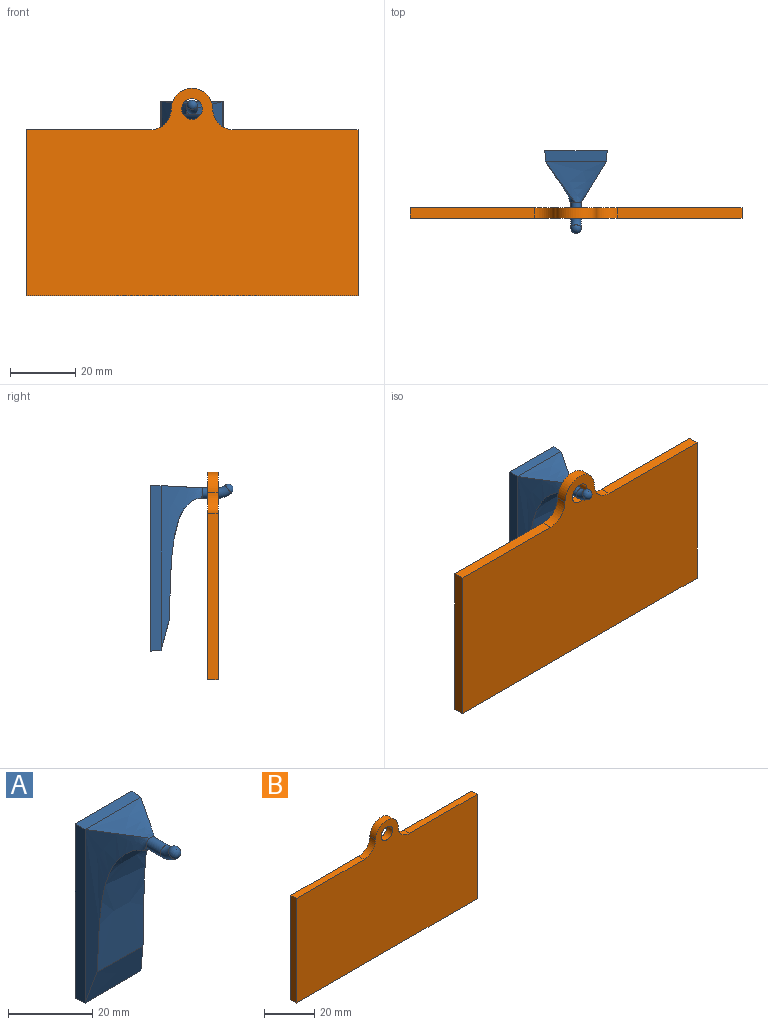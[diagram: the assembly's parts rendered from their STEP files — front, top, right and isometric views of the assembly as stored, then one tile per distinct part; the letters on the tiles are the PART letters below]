
ASSEMBLY  parts=2 mates=1
PART A: 15 faces, bbox 19.1x25.3x51.1 mm
  f0: cylinder r=1.59mm len=4.76mm, axis (0,1,0), area 47.5mm2, adj f1,f3,f4,f6,f7,f13
  f1: torus R=4.76mm, axis (1,0,0), area 33.6mm2, adj f0,f2
  f2: sphere r=1.59mm, area 16.1mm2, adj f1
  f3: bspline ~50.47x12.7mm, area 236.2mm2, adj f0,f5,f7,f9,f13,f14
  f4: bspline ~50.47x12.7mm, area 245mm2, adj f0,f5,f6,f11,f13,f14
  f5: bspline ~18.72x9.53mm, area 164.7mm2, adj f3,f4,f8,f14
  f6: bspline ~2.54x1.96mm, area 1mm2, adj f0,f4,f14
  f7: bspline ~46.7x12.7mm, area 0mm2, adj f0,f3,f14
  f8: plane 19.05x3.18mm, normal (0,-0.05,-1), area 60mm2, adj f5,f9,f11,f12
  f9: plane 50.8x3.18mm, normal (1,-0.05,0), area 161mm2, adj f3,f8,f10,f12
  f10: plane 19.05x3.18mm, normal (0,-0.05,1), area 60mm2, adj f9,f11,f12,f13
  f11: plane 50.8x3.18mm, normal (-1,-0.05,0), area 161mm2, adj f4,f8,f10,f12
  f12: plane 50.8x19.05mm, normal (0,1,0), area 967.7mm2, adj f8,f9,f10,f11
  f13: bspline ~18.72x12.7mm, area 132.7mm2, adj f0,f3,f4,f10
  f14: extruded ~37.4x15.38mm, area 532.5mm2, adj f3,f4,f5,f6,f7
PART B: 11 faces, bbox 101.6x3.2x63.5 mm
  f0: cylinder r=6.35mm len=6.35mm, axis (0,1,0), area 31.7mm2, adj f1,f8,f9,f10
  f1: plane 38.1x3.18mm, normal (0,0,1), area 121mm2, adj f0,f2,f9,f10
  f2: plane 50.8x3.18mm, normal (-1,0,0), area 161.3mm2, adj f1,f3,f9,f10
  f3: plane 101.6x3.18mm, normal (0,0,-1), area 322.6mm2, adj f2,f4,f9,f10
  f4: plane 50.8x3.18mm, normal (1,0,0), area 161.3mm2, adj f3,f5,f9,f10
  f5: plane 38.1x3.18mm, normal (0,0,1), area 121mm2, adj f4,f6,f9,f10
  f6: cylinder r=6.35mm len=6.35mm, axis (0,1,0), area 31.7mm2, adj f5,f8,f9,f10
  f7: cylinder r=3.17mm len=6.35mm, axis (0,1,0), area 63.3mm2, adj f9,f10
  f8: cylinder r=6.35mm len=12.7mm, axis (0,1,0), area 63.3mm2, adj f0,f6,f9,f10
  f9: plane 101.6x63.5mm, normal (0,-1,0), area 5290.9mm2, adj f0,f1,f2,f3,f4,f5,f6,f7
  f10: plane 101.6x63.5mm, normal (0,1,0), area 5290.9mm2, adj f0,f1,f2,f3,f4,f5,f6,f7
PLACE A t=(2.2,3.25,-23.19)mm
PLACE B t=(2.2,-14.21,-54.3)mm
MATE cylindrical B.f7 <-> A.f0  axis (0,-1,0) through (2.2,-17.38,-0.21)mm
